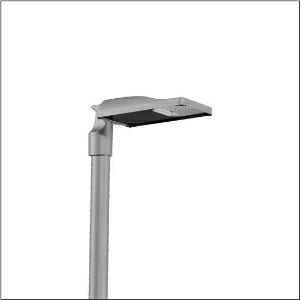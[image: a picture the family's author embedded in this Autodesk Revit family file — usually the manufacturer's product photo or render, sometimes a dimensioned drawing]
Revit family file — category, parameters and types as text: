
# Revit family: streetlight_sl_31_micro___st1_0a_5xh1d71b08da_111b
name_source: partatom
category: Lighting Fixtures
units: mm (PartAtom-declared; Revit-internal decimal feet)

## family parameters
Cut with Voids When Loaded = No
Host = Face
Light Source = No
Part Type = Normal
Room Calculation Point = No
Round Connector Dimension = Use Diameter
Shared = No

## types (1)
- --- (1 x LED, 3800 lm, 35.5 W, 2200K)
    Apparent Load = 36 VA
    CIE Flux Codes = 37 72 97 100 100
    Color Rendering = 70
    Color Temperature = 2200K
    Default Elevation = 1800 mm
    Description = Streetlight SL 31 micro Easy, LST, Desk-Remote mast luminaire for post-top, side-entry; light control with lens of PMMA; light distribution: ST1.0a, direct asymmetric distribution, for standard-compliant lighting for roads and squares; LED: luminous flux: 3.800lm, light colour: 722, colour temperature: 2200K; luminous efficacy: 107lm/W; control: pre-setting: linear dimming characteristic, flexible luminous flux parameterisation, time-dependent luminous flux control, constant luminous flux control, power reduction, intelligent temperature release in ECG and LED module, overheat protection; luminaire housing, of diecast aluminium, Siteco® metallic grey (DB 702S), corrosivity category C5 high according to DIN EN ISO 12944; cover of toughened safety glass, transparent, mast flange of diecast aluminium, Siteco® metallic grey (DB 702S), spigot size: 76/60mm, mast flange included unmounted; with cable H07RN-F 3x 1.5mm², cable length: 6,5m, connection cable pre-assembled; mains connection: 220..240V, AC, 50/60Hz; power consumption (at start of service life): 35,5W / (at end of service life): 37,5W / (with reduced operation 50%): 15,4W; protection rating (complete): IP66; insulation class (complete): insulation class II (safety insulation); impact resistance: IK10; certification: CE, ENEC, ENEC+, VDE, UKCA; permissible operating ambient temperature for outdoor applications: -40..+50°C; packaging unit: 1 piece

Light Distribution: ST1.0a
    Height = 76 mm
    Lamp = 1 x LED
    Lamp Light Flux = 3800 lm
    Lamp Power = 35.5 W
    Lamp count = 1
    Length = 467 mm
    Luminous efficacy = 107 lm/W
    Manufacturer = Siteco
    ModVariant = No
    Model = 5XH1D71B08DA
    Number of Poles = 1
    OnlyDefault = Yes
    Power Factor = 1
    Product Name = Streetlight SL 31 micro | ST1.0a
    Product group = mast luminaire | pylon top
    ProductGroupID = 6100
    Protection Class = Protection class II
    Protection Degree = IP 66
    RLX_Detail_Level = 1
    RLX_Emergency_Light_Flux = 0 lm
    RLX_Emergency_Type = 0
    RLX_Emergency_Type_DB = No
    RlxData = <blob elided: 23221 chars, md5=f6d93b24>
    Socket = socket
    Standby Power = 0 W
    System Light Flux = 3800 lm
    System Power = 36 W
    Type Comments = factory setting: luminous flux: 100 % | dim-lin: 254 | 700 mA
    Type Image = l_1300309.jpg
    URL = http://relux.com
    VarID = @adj_008939
    Voltage = 0 V
    Weight = 0.00 kg
    Width = 265 mm

## geometry (parser evidence)
native form markers: Blend x4, Sweep x10
no freeform markers — native parametric forms only
